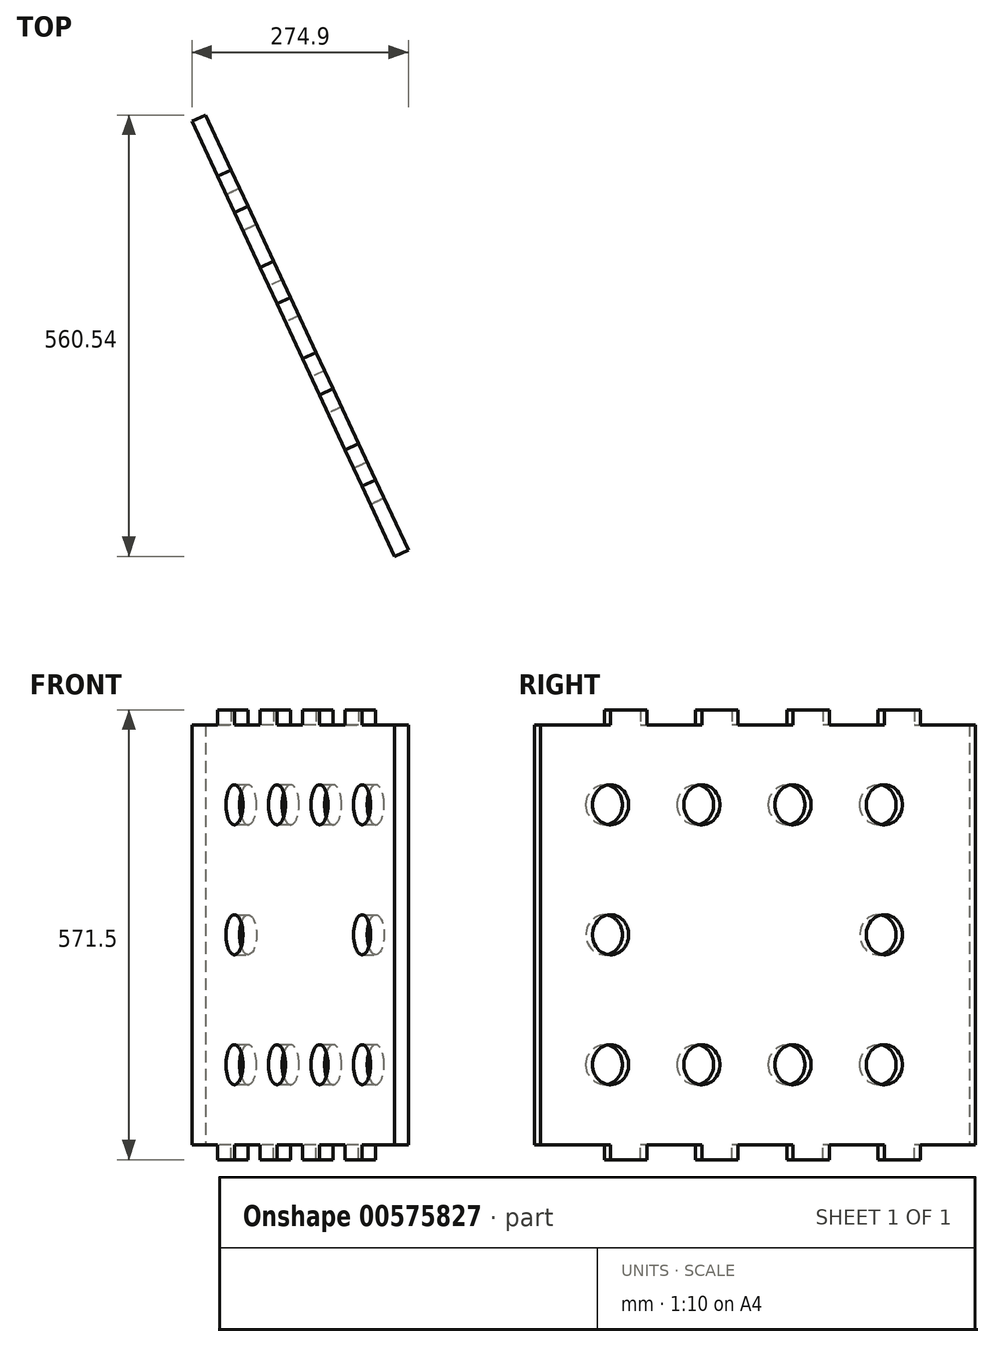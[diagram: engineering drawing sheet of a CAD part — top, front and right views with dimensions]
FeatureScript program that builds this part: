
annotation { "Feature Type Name" : "Feature", "Feature Type Description" : "" }
export const myFeature = defineFeature(function(context is Context, id is Id, definition is map)
    precondition{}
    {
        {
            var Q0;
            Q0=qCreatedBy(makeId("Top.planeOp"),FACE);
            var sketch = newSketch(context, id + "F0", { "sketchPlane" : qUnion([Q0])});
            skLineSegment(sketch, "E0", {"start": v(0, 0) * mm, "end": v(17.27, 8.05) * mm});
            skLineSegment(sketch, "E1", {"start": v(17.27, 8.05) * mm, "end": v(-240.36, 560.54) * mm});
            skLineSegment(sketch, "E2", {"start": v(-240.36, 560.54) * mm, "end": v(-257.63, 552.49) * mm});
            skLineSegment(sketch, "E3", {"start": v(-257.63, 552.49) * mm, "end": v(0, 0) * mm});
            skSolve(sketch);
        }
        {
            var Q0;
            Q0 = qSketchRegion(id + "F0", true);
            extrude(context, id + "F1", {"entities" : qUnion([Q0]), "depth" : 533.4 * mm, "offsetDistance" : 25.4 * mm});
        }
        {
            var Q0;
            Q0=makeQuery(id+"F1.opExtrude","CAP_FACE",FACE,{"disambiguationData":[OSD([sQuery(id+"F0.wireOp",EDGE,"E0"),sQuery(id+"F0.wireOp",EDGE,"E1"),sQuery(id+"F0.wireOp",EDGE,"E2"),sQuery(id+"F0.wireOp",EDGE,"E3")])],"isStart":true});
            var sketch = newSketch(context, id + "F2", { "sketchPlane" : qUnion([Q0])});
            skLineSegment(sketch, "E4", {"start": v(-207.8, -490.69) * mm, "end": v(-225.06, -482.64) * mm});
            skLineSegment(sketch, "E5", {"start": v(-225.06, -482.64) * mm, "end": v(-203.59, -436.6) * mm});
            skLineSegment(sketch, "E6", {"start": v(-203.59, -436.6) * mm, "end": v(-186.32, -444.65) * mm});
            skLineSegment(sketch, "E7", {"start": v(-186.32, -444.65) * mm, "end": v(-207.8, -490.69) * mm});
            skLineSegment(sketch, "E8", {"start": v(-153.75, -374.8) * mm, "end": v(-171.02, -366.74) * mm});
            skLineSegment(sketch, "E9", {"start": v(-171.02, -366.74) * mm, "end": v(-149.55, -320.7) * mm});
            skLineSegment(sketch, "E10", {"start": v(-149.55, -320.7) * mm, "end": v(-132.28, -328.76) * mm});
            skLineSegment(sketch, "E11", {"start": v(-132.28, -328.76) * mm, "end": v(-153.75, -374.8) * mm});
            skLineSegment(sketch, "E12", {"start": v(-78.24, -212.86) * mm, "end": v(-99.71, -258.9) * mm});
            skLineSegment(sketch, "E13", {"start": v(-99.71, -258.9) * mm, "end": v(-116.98, -250.85) * mm});
            skLineSegment(sketch, "E14", {"start": v(-116.98, -250.85) * mm, "end": v(-95.5, -204.81) * mm});
            skLineSegment(sketch, "E15", {"start": v(-95.5, -204.81) * mm, "end": v(-78.24, -212.86) * mm});
            skLineSegment(sketch, "E16", {"start": v(-45.67, -143.01) * mm, "end": v(-62.93, -134.96) * mm});
            skLineSegment(sketch, "E17", {"start": v(-62.93, -134.96) * mm, "end": v(-41.47, -88.92) * mm});
            skLineSegment(sketch, "E18", {"start": v(-41.47, -88.92) * mm, "end": v(-24.2, -96.97) * mm});
            skLineSegment(sketch, "E19", {"start": v(-24.2, -96.97) * mm, "end": v(-45.67, -143.01) * mm});
            skSolve(sketch);
        }
        {
            var Q0;
            Q0=makeQuery(id+"F2.imprint","IMPRINT",FACE,{"disambiguationData":[TD([[makeQuery(id+"F2.imprint","IMPRINT",EDGE,{"derivedFrom":sQuery(id+"F2.wireOp",EDGE,"E4")}),-1.0]])]});
            var Q1;
            Q1=makeQuery(id+"F2.imprint","IMPRINT",FACE,{"disambiguationData":[TD([[makeQuery(id+"F2.imprint","IMPRINT",EDGE,{"derivedFrom":sQuery(id+"F2.wireOp",EDGE,"E8")}),-1.0]])]});
            var Q2;
            Q2=makeQuery(id+"F2.imprint","IMPRINT",FACE,{"disambiguationData":[TD([[makeQuery(id+"F2.imprint","IMPRINT",EDGE,{"derivedFrom":sQuery(id+"F2.wireOp",EDGE,"E12")}),-1.0]])]});
            var Q3;
            Q3=makeQuery(id+"F2.imprint","IMPRINT",FACE,{"disambiguationData":[TD([[makeQuery(id+"F2.imprint","IMPRINT",EDGE,{"derivedFrom":sQuery(id+"F2.wireOp",EDGE,"E16")}),-1.0]])]});
            extrude(context, id + "F3", {"entities" : qUnion([Q0, Q1, Q2, Q3]), "operationType" : NewBodyOperationType.ADD, "depth" : 19.05 * mm, "offsetDistance" : 25.4 * mm});
        }
        {
            var Q0;
            Q0=makeQuery(id+"F1.opExtrude","CAP_FACE",FACE,{"disambiguationData":[OSD([sQuery(id+"F0.wireOp",EDGE,"E0"),sQuery(id+"F0.wireOp",EDGE,"E1"),sQuery(id+"F0.wireOp",EDGE,"E2"),sQuery(id+"F0.wireOp",EDGE,"E3")])],"isStart":false});
            var sketch = newSketch(context, id + "F4", { "sketchPlane" : qUnion([Q0])});
            skLineSegment(sketch, "E20", {"start": v(-225.06, 482.64) * mm, "end": v(-207.8, 490.69) * mm});
            skLineSegment(sketch, "E21", {"start": v(-207.8, 490.69) * mm, "end": v(-186.32, 444.65) * mm});
            skLineSegment(sketch, "E22", {"start": v(-186.32, 444.65) * mm, "end": v(-203.59, 436.6) * mm});
            skLineSegment(sketch, "E23", {"start": v(-203.59, 436.6) * mm, "end": v(-225.06, 482.64) * mm});
            skLineSegment(sketch, "E24", {"start": v(-149.55, 320.7) * mm, "end": v(-132.28, 328.76) * mm});
            skLineSegment(sketch, "E25", {"start": v(-132.28, 328.76) * mm, "end": v(-153.75, 374.8) * mm});
            skLineSegment(sketch, "E26", {"start": v(-153.75, 374.8) * mm, "end": v(-171.02, 366.74) * mm});
            skLineSegment(sketch, "E27", {"start": v(-171.02, 366.74) * mm, "end": v(-149.55, 320.7) * mm});
            skLineSegment(sketch, "E28", {"start": v(-99.71, 258.9) * mm, "end": v(-116.98, 250.85) * mm});
            skLineSegment(sketch, "E29", {"start": v(-116.98, 250.85) * mm, "end": v(-95.5, 204.81) * mm});
            skLineSegment(sketch, "E30", {"start": v(-95.5, 204.81) * mm, "end": v(-78.24, 212.86) * mm});
            skLineSegment(sketch, "E31", {"start": v(-78.24, 212.86) * mm, "end": v(-99.71, 258.9) * mm});
            skLineSegment(sketch, "E32", {"start": v(-45.67, 143.01) * mm, "end": v(-24.2, 96.97) * mm});
            skLineSegment(sketch, "E33", {"start": v(-24.2, 96.97) * mm, "end": v(-41.47, 88.92) * mm});
            skLineSegment(sketch, "E34", {"start": v(-41.47, 88.92) * mm, "end": v(-62.93, 134.96) * mm});
            skLineSegment(sketch, "E35", {"start": v(-62.93, 134.96) * mm, "end": v(-45.67, 143.01) * mm});
            skSolve(sketch);
        }
        {
            var Q0;
            Q0 = qSketchRegion(id + "F4", true);
            extrude(context, id + "F5", {"entities" : qUnion([Q0]), "operationType" : NewBodyOperationType.ADD, "depth" : 19.05 * mm, "offsetDistance" : 25.4 * mm});
        }
        {
            var Q0;
            Q0=makeQuery(id+"F0.imprint","IMPRINT",FACE,{"disambiguationData":[TD([[makeQuery(id+"F0.imprint","IMPRINT",EDGE,{"derivedFrom":sQuery(id+"F0.wireOp",EDGE,"E0")}),1.0]])]});
            var sketch = newSketch(context, id + "F6", { "sketchPlane" : qUnion([Q0])});
            skLineSegment(sketch, "E36.bottom", {"start": v(17.27, 0) * mm, "end": v(-257.63, 0) * mm});
            skLineSegment(sketch, "E36.top", {"start": v(17.27, 560.54) * mm, "end": v(-257.63, 560.54) * mm});
            skLineSegment(sketch, "E36.left", {"start": v(17.27, 0) * mm, "end": v(17.27, 560.54) * mm});
            skLineSegment(sketch, "E36.right", {"start": v(-257.63, 0) * mm, "end": v(-257.63, 560.54) * mm});
            skLineSegment(sketch, "E37", {"start": v(-41.47, 88.92) * mm, "end": v(-24.2, 96.97) * mm});
            skLineSegment(sketch, "E38", {"start": v(-24.2, 96.97) * mm, "end": v(-45.67, 143.01) * mm});
            skLineSegment(sketch, "E39", {"start": v(-45.67, 143.01) * mm, "end": v(-62.93, 134.96) * mm});
            skLineSegment(sketch, "E40", {"start": v(-62.93, 134.96) * mm, "end": v(-41.47, 88.92) * mm});
            skLineSegment(sketch, "E41", {"start": v(-95.5, 204.81) * mm, "end": v(-78.24, 212.86) * mm});
            skLineSegment(sketch, "E42", {"start": v(-78.24, 212.86) * mm, "end": v(-99.71, 258.9) * mm});
            skLineSegment(sketch, "E43", {"start": v(-99.71, 258.9) * mm, "end": v(-116.98, 250.85) * mm});
            skLineSegment(sketch, "E44", {"start": v(-116.98, 250.85) * mm, "end": v(-95.5, 204.81) * mm});
            skLineSegment(sketch, "E45", {"start": v(-149.55, 320.7) * mm, "end": v(-132.28, 328.76) * mm});
            skLineSegment(sketch, "E46", {"start": v(-132.28, 328.76) * mm, "end": v(-153.75, 374.8) * mm});
            skLineSegment(sketch, "E47", {"start": v(-153.75, 374.8) * mm, "end": v(-171.02, 366.74) * mm});
            skLineSegment(sketch, "E48", {"start": v(-171.02, 366.74) * mm, "end": v(-149.55, 320.7) * mm});
            skLineSegment(sketch, "E49", {"start": v(-203.59, 436.6) * mm, "end": v(-186.32, 444.65) * mm});
            skLineSegment(sketch, "E50", {"start": v(-186.32, 444.65) * mm, "end": v(-207.8, 490.69) * mm});
            skLineSegment(sketch, "E51", {"start": v(-207.8, 490.69) * mm, "end": v(-225.06, 482.64) * mm});
            skLineSegment(sketch, "E52", {"start": v(-225.06, 482.64) * mm, "end": v(-203.59, 436.6) * mm});
            skSolve(sketch);
        }
        {
            var Q0;
            Q0=makeQuery(id+"F5.boolean.opBoolean","MERGE",FACE,{"derivedFrom":[makeQuery(id+"F3.boolean.opBoolean","MERGE",FACE,{"derivedFrom":[makeQuery(id+"F1.opExtrude","SWEPT_FACE",FACE,{"disambiguationData":[OSD([sQuery(id+"F0.wireOp",EDGE,"E3")])]}),makeQuery(id+"F3.opExtrude","SWEPT_FACE",FACE,{"disambiguationData":[OSD([sQuery(id+"F2.wireOp",EDGE,"E5")])]}),makeQuery(id+"F3.opExtrude","SWEPT_FACE",FACE,{"disambiguationData":[OSD([sQuery(id+"F2.wireOp",EDGE,"E9")])]}),makeQuery(id+"F3.opExtrude","SWEPT_FACE",FACE,{"disambiguationData":[OSD([sQuery(id+"F2.wireOp",EDGE,"E14")])]}),makeQuery(id+"F3.opExtrude","SWEPT_FACE",FACE,{"disambiguationData":[OSD([sQuery(id+"F2.wireOp",EDGE,"E17")])]})]}),makeQuery(id+"F5.opExtrude","SWEPT_FACE",FACE,{"disambiguationData":[OSD([sQuery(id+"F4.wireOp",EDGE,"E23")])]}),makeQuery(id+"F5.opExtrude","SWEPT_FACE",FACE,{"disambiguationData":[OSD([sQuery(id+"F4.wireOp",EDGE,"E27")])]}),makeQuery(id+"F5.opExtrude","SWEPT_FACE",FACE,{"disambiguationData":[OSD([sQuery(id+"F4.wireOp",EDGE,"E29")])]}),makeQuery(id+"F5.opExtrude","SWEPT_FACE",FACE,{"disambiguationData":[OSD([sQuery(id+"F4.wireOp",EDGE,"E34")])]})]});
            var sketch = newSketch(context, id + "F7", { "sketchPlane" : qUnion([Q0])});
            skCircle(sketch, "E53", {"center": v(-98.12, 431.8) * mm, "radius": 25.4 * mm});
            skCircle(sketch, "E54", {"center": v(-98.12, 101.6) * mm, "radius": 25.4 * mm});
            skCircle(sketch, "E55", {"center": v(-353.86, 101.6) * mm, "radius": 25.4 * mm});
            skCircle(sketch, "E56", {"center": v(-481.73, 101.6) * mm, "radius": 25.4 * mm});
            skCircle(sketch, "E57", {"center": v(-225.99, 101.6) * mm, "radius": 25.4 * mm});
            skCircle(sketch, "E58", {"center": v(-225.99, 431.8) * mm, "radius": 25.4 * mm});
            skCircle(sketch, "E59", {"center": v(-353.86, 431.8) * mm, "radius": 25.4 * mm});
            skCircle(sketch, "E60", {"center": v(-481.73, 431.8) * mm, "radius": 25.4 * mm});
            skSolve(sketch);
        }
        {
            var Q0;
            Q0 = qSketchRegion(id + "F7", true);
            extrude(context, id + "F8", {"entities" : qUnion([Q0]), "operationType" : NewBodyOperationType.REMOVE, "oppositeDirection" : true, "depth" : 19.05 * mm, "offsetDistance" : 25.4 * mm});
        }
        {
            var Q0;
            Q0=makeQuery(id+"F5.boolean.opBoolean","MERGE",FACE,{"derivedFrom":[makeQuery(id+"F3.boolean.opBoolean","MERGE",FACE,{"derivedFrom":[makeQuery(id+"F1.opExtrude","SWEPT_FACE",FACE,{"disambiguationData":[OSD([sQuery(id+"F0.wireOp",EDGE,"E1")])]}),makeQuery(id+"F3.opExtrude","SWEPT_FACE",FACE,{"disambiguationData":[OSD([sQuery(id+"F2.wireOp",EDGE,"E7")])]}),makeQuery(id+"F3.opExtrude","SWEPT_FACE",FACE,{"disambiguationData":[OSD([sQuery(id+"F2.wireOp",EDGE,"E11")])]}),makeQuery(id+"F3.opExtrude","SWEPT_FACE",FACE,{"disambiguationData":[OSD([sQuery(id+"F2.wireOp",EDGE,"E12")])]}),makeQuery(id+"F3.opExtrude","SWEPT_FACE",FACE,{"disambiguationData":[OSD([sQuery(id+"F2.wireOp",EDGE,"E19")])]})]}),makeQuery(id+"F5.opExtrude","SWEPT_FACE",FACE,{"disambiguationData":[OSD([sQuery(id+"F4.wireOp",EDGE,"E21")])]}),makeQuery(id+"F5.opExtrude","SWEPT_FACE",FACE,{"disambiguationData":[OSD([sQuery(id+"F4.wireOp",EDGE,"E25")])]}),makeQuery(id+"F5.opExtrude","SWEPT_FACE",FACE,{"disambiguationData":[OSD([sQuery(id+"F4.wireOp",EDGE,"E31")])]}),makeQuery(id+"F5.opExtrude","SWEPT_FACE",FACE,{"disambiguationData":[OSD([sQuery(id+"F4.wireOp",EDGE,"E32")])]})]});
            var sketch = newSketch(context, id + "F9", { "sketchPlane" : qUnion([Q0])});
            skCircle(sketch, "E61", {"center": v(481.73, 266.7) * mm, "radius": 25.4 * mm});
            skPoint(sketch, "E61.centerSnap0", {"position": v(0, 266.7) * mm});
            skCircle(sketch, "E62", {"center": v(98.12, 266.7) * mm, "radius": 25.4 * mm});
            skSolve(sketch);
        }
        {
            var Q0;
            Q0 = qSketchRegion(id + "F9", true);
            extrude(context, id + "F10", {"entities" : qUnion([Q0]), "operationType" : NewBodyOperationType.REMOVE, "oppositeDirection" : true, "depth" : 25.4 * mm, "offsetDistance" : 25.4 * mm});
        }
    });
